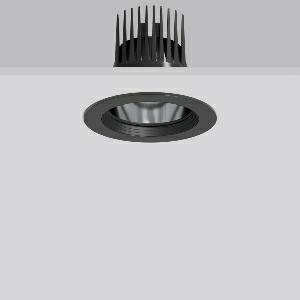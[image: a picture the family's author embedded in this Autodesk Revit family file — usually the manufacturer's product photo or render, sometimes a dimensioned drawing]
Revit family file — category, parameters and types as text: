
# Revit family: heledon_maxi_e_901772_003_76_f125
name_source: partatom
category: Lighting Fixtures
units: mm (PartAtom-declared; Revit-internal decimal feet)

## family parameters
Cut with Voids When Loaded = No
Host = Face
Light Source = No
Part Type = Normal
Room Calculation Point = No
Round Connector Dimension = Use Diameter
Shared = No

## types (1)
- HELEDON maxi E (1 x LED Modul 932 fresh meat, 2150 lm, 3200)
    Apparent Load = 33 VA
    Approval mark = CE
    CIE Flux Codes = 100 100 100 100 100
    Color Rendering = 90
    Color Temperature = 3200
    Default Elevation = 1800 mm
    Description = Series: HELEDON maxi
Round recessed downlight. Housing: die-cast aluminium, powder-coated. Black plastic ring and recessed LED to prevent glare from the side. Optical assembly with reflector made of MIRO-Silver with 98% total light reflection for outstanding efficiency - can be changed without tools. Special LED for illumination of meat included. Suitable for Recessed ceiling mounting. Installation without tools thanks to spring fastening system. Including separate LED converter with connecting cable 600 mm.High quality converter without flickering and stroboscopic effect. Through-wiring box (5 pole) available as accessory. The following accessories can be mounted without use of tools: interchangeable lenses, decorative glasses, honeycomb louvre, clear and frosted diffusers, white interchangeable plastic ring. 
Colour: deep black, matt (RAL 9005)
Diameter: 162 mm
Height: 3 mm
Cut-out diameter: 152 mm
Recess height: 200 mm
Luminaire: recess height: 135 mm
Lamp: LED
Socket: without socket
Colour temperature: fresh meat
System power: 33 W
Rated luminous flux: 2150 lm
Luminous efficiency: 65 lm/W
Control gear: Converter, dimmable, DALI
Protection class: II
Type of protection: IP 20
    Height = 0 mm  [stored 0 ft]
    Lamp = 1 x LED Modul 932 fresh meat
    Lamp Light Flux = 2150 lm
    Lamp count = 1
    Length = 162 mm
    Lifetime = 50000 h
    Luminous efficacy = 65 lm/W
    Manufacturer = RZB
    ModVariant = No
    Model = 901772.003.76
    Mounting Place = Ceiling
    Mounting Type = Recessed
    Number of Poles = 1
    OnlyDefault = Yes
    Power Factor = 1
    Product Name = HELEDON maxi E
    Product group = Recessed downlights
    ProductGroupID = 402
    Protection Class = Protection class II
    Protection Degree = IP 20
    RLX_Detail_Level = 1
    RLX_Emergency_Light_Flux = 0 lm
    RLX_Emergency_Type = 0
    RLX_Emergency_Type_DB = No
    RlxData = <blob elided: 123101 chars, md5=0b5bad1d>
    Socket = socket
    Standby Power = 0 W
    System Light Flux = 2150 lm
    System Power = 33 W
    Type Comments = Product without accessories
    Type Image = 901662.003.jpg
    URL = http://relux.com
    VarID = ---
    Voltage = 230 V
    Voltage Range = 220-240 V
    Weight = 0.00 kg
    Width = 0 mm  [stored 0 ft]

note: [stored X ft] marks values corroborated as IEEE doubles in the binary element streams (Revit-internal decimal feet)

## geometry (parser evidence)
native form markers: Blend x4, Sweep x12
no freeform markers — native parametric forms only
